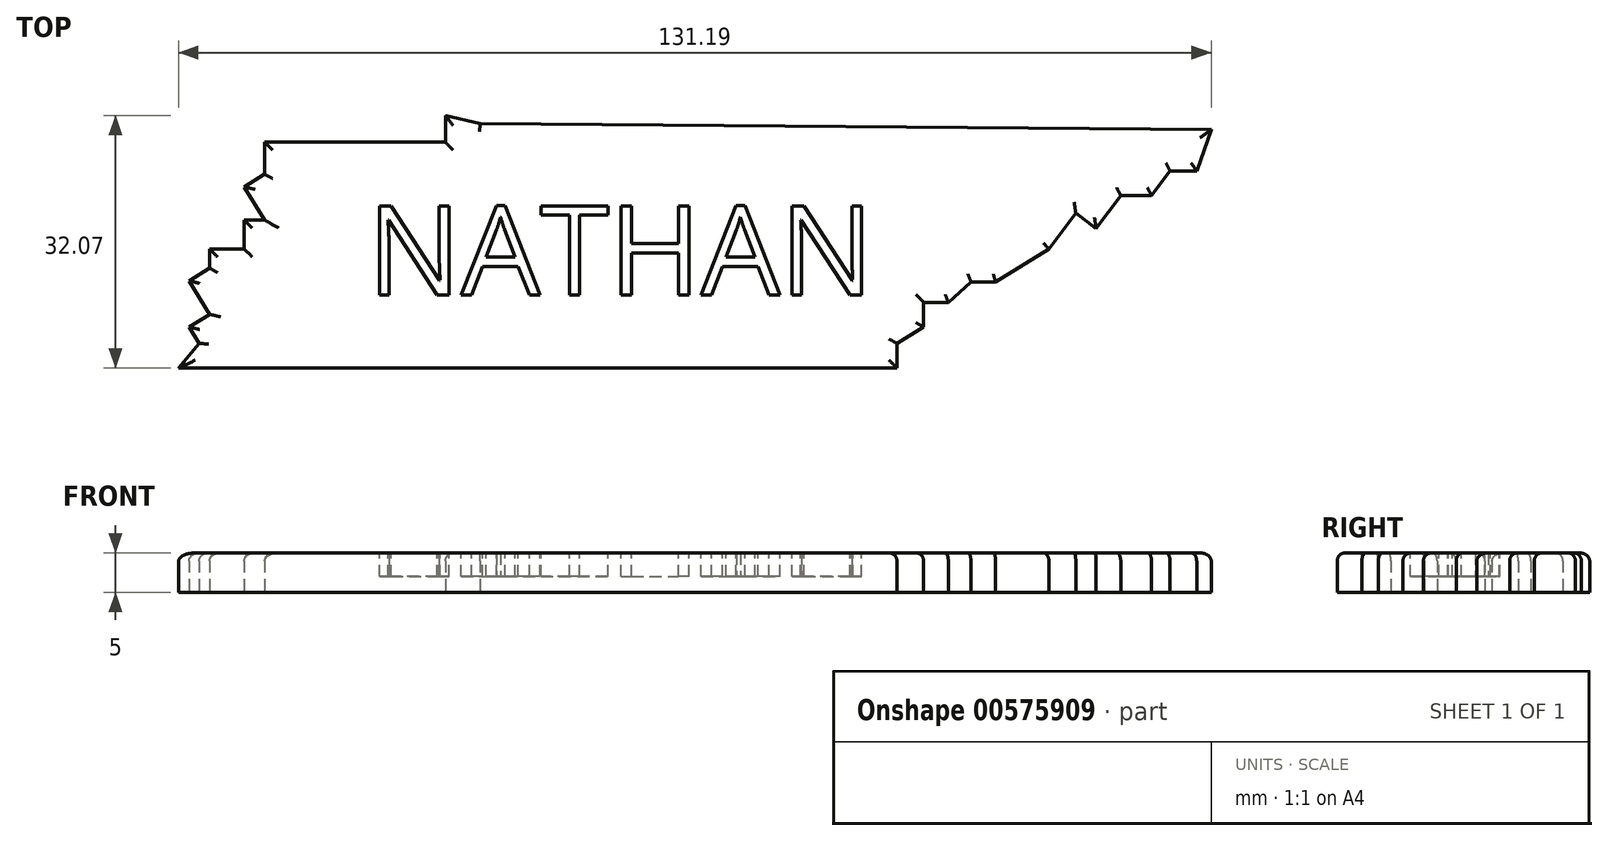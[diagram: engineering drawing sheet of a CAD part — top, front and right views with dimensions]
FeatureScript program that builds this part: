
annotation { "Feature Type Name" : "Feature", "Feature Type Description" : "" }
export const myFeature = defineFeature(function(context is Context, id is Id, definition is map)
    precondition{}
    {
        {
            var Q0;
            Q0=qCreatedBy(makeId("Top.planeOp"),FACE);
            var sketch = newSketch(context, id + "F0", { "sketchPlane" : qUnion([Q0])});
            skLineSegment(sketch, "E0", {"start": v(64.67, 9.9) * mm, "end": v(61.28, 9.9) * mm});
            skLineSegment(sketch, "E1", {"start": v(61.28, 9.9) * mm, "end": v(58.93, 6.78) * mm});
            skLineSegment(sketch, "E2", {"start": v(58.93, 6.78) * mm, "end": v(55.02, 6.78) * mm});
            skLineSegment(sketch, "E3", {"start": v(55.02, 6.78) * mm, "end": v(51.9, 2.6) * mm});
            skLineSegment(sketch, "E4", {"start": v(51.9, 2.6) * mm, "end": v(49.3, 4.55) * mm});
            skLineSegment(sketch, "E5", {"start": v(49.3, 4.55) * mm, "end": v(45.9, 0) * mm});
            skLineSegment(sketch, "E6", {"start": v(45.9, 0) * mm, "end": v(42.5, -2.09) * mm});
            skLineSegment(sketch, "E7", {"start": v(42.5, -2.09) * mm, "end": v(39.11, -4.17) * mm});
            skLineSegment(sketch, "E8", {"start": v(39.11, -4.17) * mm, "end": v(35.99, -4.17) * mm});
            skLineSegment(sketch, "E9", {"start": v(35.99, -4.17) * mm, "end": v(33.12, -6.78) * mm});
            skLineSegment(sketch, "E10", {"start": v(33.12, -6.78) * mm, "end": v(29.99, -6.78) * mm});
            skLineSegment(sketch, "E11", {"start": v(29.99, -6.78) * mm, "end": v(29.99, -9.9) * mm});
            skLineSegment(sketch, "E12", {"start": v(29.99, -9.9) * mm, "end": v(26.6, -12) * mm});
            skLineSegment(sketch, "E13", {"start": v(26.6, -12) * mm, "end": v(26.6, -15.12) * mm});
            skLineSegment(sketch, "E14", {"start": v(26.6, -15.12) * mm, "end": v(-64.67, -15.12) * mm});
            skLineSegment(sketch, "E15", {"start": v(-64.67, -15.12) * mm, "end": v(-62.06, -12) * mm});
            skLineSegment(sketch, "E16", {"start": v(-62.06, -12) * mm, "end": v(-63.35, -9.9) * mm});
            skLineSegment(sketch, "E17", {"start": v(-63.35, -9.9) * mm, "end": v(-60.73, -8.3) * mm});
            skLineSegment(sketch, "E18", {"start": v(-60.73, -8.3) * mm, "end": v(-63.35, -4.04) * mm});
            skLineSegment(sketch, "E19", {"start": v(-63.35, -4.04) * mm, "end": v(-60.73, -2.43) * mm});
            skLineSegment(sketch, "E20", {"start": v(-60.73, -2.43) * mm, "end": v(-60.73, 0) * mm});
            skLineSegment(sketch, "E21", {"start": v(-60.73, 0) * mm, "end": v(-56.32, 0) * mm});
            skLineSegment(sketch, "E22", {"start": v(-56.32, 0) * mm, "end": v(-56.32, 3.65) * mm});
            skLineSegment(sketch, "E23", {"start": v(-56.32, 3.65) * mm, "end": v(-53.72, 3.65) * mm});
            skLineSegment(sketch, "E24", {"start": v(-53.72, 3.65) * mm, "end": v(-55.02, 5.77) * mm});
            skLineSegment(sketch, "E25", {"start": v(-55.02, 5.77) * mm, "end": v(-56.32, 7.89) * mm});
            skLineSegment(sketch, "E26", {"start": v(-56.32, 7.89) * mm, "end": v(-53.72, 9.5) * mm});
            skLineSegment(sketch, "E27", {"start": v(-53.72, 9.5) * mm, "end": v(-53.72, 13.56) * mm});
            skLineSegment(sketch, "E28", {"start": v(-53.72, 13.56) * mm, "end": v(-30.77, 13.56) * mm});
            skLineSegment(sketch, "E29", {"start": v(-30.77, 13.56) * mm, "end": v(-30.77, 16.95) * mm});
            skLineSegment(sketch, "E30", {"start": v(-30.77, 16.95) * mm, "end": v(-26.34, 15.9) * mm});
            skLineSegment(sketch, "E31", {"start": v(64.67, 9.9) * mm, "end": v(66.52, 15.14) * mm});
            skLineSegment(sketch, "E32", {"start": v(66.52, 15.14) * mm, "end": v(-26.34, 15.9) * mm});
            skSolve(sketch);
        }
        {
            var Q0;
            Q0=makeQuery(id+"F0.imprint","IMPRINT",FACE,{"disambiguationData":[TD([[makeQuery(id+"F0.imprint","IMPRINT",EDGE,{"derivedFrom":sQuery(id+"F0.wireOp",EDGE,"E0")}),-1.0]])]});
            extrude(context, id + "F1", {"entities" : qUnion([Q0]), "depth" : 5 * mm, "offsetDistance" : 25 * mm});
        }
        {
            var Q0;
            Q0=makeQuery(id+"F1.opExtrude","CAP_EDGE",EDGE,{"disambiguationData":[OSD([sQuery(id+"F0.wireOp",EDGE,"E30")])],"isStart":false});
            var Q1;
            Q1=makeQuery(id+"F1.opExtrude","CAP_EDGE",EDGE,{"disambiguationData":[OSD([sQuery(id+"F0.wireOp",EDGE,"E28")])],"isStart":false});
            var Q2;
            Q2=makeQuery(id+"F1.opExtrude","CAP_EDGE",EDGE,{"disambiguationData":[OSD([sQuery(id+"F0.wireOp",EDGE,"E27")])],"isStart":false});
            var Q3;
            Q3=makeQuery(id+"F1.opExtrude","CAP_EDGE",EDGE,{"disambiguationData":[OSD([sQuery(id+"F0.wireOp",EDGE,"E26")])],"isStart":false});
            var Q4;
            Q4=makeQuery(id+"F1.opExtrude","CAP_EDGE",EDGE,{"disambiguationData":[OSD([sQuery(id+"F0.wireOp",EDGE,"E24"),sQuery(id+"F0.wireOp",EDGE,"E25")])],"isStart":false});
            var Q5;
            Q5=makeQuery(id+"F1.opExtrude","CAP_EDGE",EDGE,{"disambiguationData":[OSD([sQuery(id+"F0.wireOp",EDGE,"E29")])],"isStart":false});
            var Q6;
            Q6=makeQuery(id+"F1.opExtrude","CAP_EDGE",EDGE,{"disambiguationData":[OSD([sQuery(id+"F0.wireOp",EDGE,"E32")])],"isStart":false});
            var Q7;
            Q7=makeQuery(id+"F1.opExtrude","CAP_EDGE",EDGE,{"disambiguationData":[OSD([sQuery(id+"F0.wireOp",EDGE,"E23")])],"isStart":false});
            var Q8;
            Q8=makeQuery(id+"F1.opExtrude","CAP_EDGE",EDGE,{"disambiguationData":[OSD([sQuery(id+"F0.wireOp",EDGE,"E22")])],"isStart":false});
            var Q9;
            Q9=makeQuery(id+"F1.opExtrude","CAP_EDGE",EDGE,{"disambiguationData":[OSD([sQuery(id+"F0.wireOp",EDGE,"E21")])],"isStart":false});
            var Q10;
            Q10=makeQuery(id+"F1.opExtrude","CAP_EDGE",EDGE,{"disambiguationData":[OSD([sQuery(id+"F0.wireOp",EDGE,"E20")])],"isStart":false});
            var Q11;
            Q11=makeQuery(id+"F1.opExtrude","CAP_EDGE",EDGE,{"disambiguationData":[OSD([sQuery(id+"F0.wireOp",EDGE,"E19")])],"isStart":false});
            var Q12;
            Q12=makeQuery(id+"F1.opExtrude","CAP_EDGE",EDGE,{"disambiguationData":[OSD([sQuery(id+"F0.wireOp",EDGE,"E18")])],"isStart":false});
            var Q13;
            Q13=makeQuery(id+"F1.opExtrude","CAP_EDGE",EDGE,{"disambiguationData":[OSD([sQuery(id+"F0.wireOp",EDGE,"E17")])],"isStart":false});
            var Q14;
            Q14=makeQuery(id+"F1.opExtrude","CAP_EDGE",EDGE,{"disambiguationData":[OSD([sQuery(id+"F0.wireOp",EDGE,"E16")])],"isStart":false});
            var Q15;
            Q15=makeQuery(id+"F1.opExtrude","CAP_EDGE",EDGE,{"disambiguationData":[OSD([sQuery(id+"F0.wireOp",EDGE,"E15")])],"isStart":false});
            var Q16;
            Q16=makeQuery(id+"F1.opExtrude","CAP_EDGE",EDGE,{"disambiguationData":[OSD([sQuery(id+"F0.wireOp",EDGE,"E14")])],"isStart":false});
            var Q17;
            Q17=makeQuery(id+"F1.opExtrude","CAP_EDGE",EDGE,{"disambiguationData":[OSD([sQuery(id+"F0.wireOp",EDGE,"E13")])],"isStart":false});
            var Q18;
            Q18=makeQuery(id+"F1.opExtrude","CAP_EDGE",EDGE,{"disambiguationData":[OSD([sQuery(id+"F0.wireOp",EDGE,"E12")])],"isStart":false});
            var Q19;
            Q19=makeQuery(id+"F1.opExtrude","CAP_EDGE",EDGE,{"disambiguationData":[OSD([sQuery(id+"F0.wireOp",EDGE,"E11")])],"isStart":false});
            var Q20;
            Q20=makeQuery(id+"F1.opExtrude","CAP_EDGE",EDGE,{"disambiguationData":[OSD([sQuery(id+"F0.wireOp",EDGE,"E10")])],"isStart":false});
            var Q21;
            Q21=makeQuery(id+"F1.opExtrude","CAP_EDGE",EDGE,{"disambiguationData":[OSD([sQuery(id+"F0.wireOp",EDGE,"E9")])],"isStart":false});
            var Q22;
            Q22=makeQuery(id+"F1.opExtrude","CAP_EDGE",EDGE,{"disambiguationData":[OSD([sQuery(id+"F0.wireOp",EDGE,"E8")])],"isStart":false});
            var Q23;
            Q23=makeQuery(id+"F1.opExtrude","CAP_EDGE",EDGE,{"disambiguationData":[OSD([sQuery(id+"F0.wireOp",EDGE,"E6"),sQuery(id+"F0.wireOp",EDGE,"E7")])],"isStart":false});
            var Q24;
            Q24=makeQuery(id+"F1.opExtrude","CAP_EDGE",EDGE,{"disambiguationData":[OSD([sQuery(id+"F0.wireOp",EDGE,"E5")])],"isStart":false});
            var Q25;
            Q25=makeQuery(id+"F1.opExtrude","CAP_EDGE",EDGE,{"disambiguationData":[OSD([sQuery(id+"F0.wireOp",EDGE,"E4")])],"isStart":false});
            var Q26;
            Q26=makeQuery(id+"F1.opExtrude","CAP_EDGE",EDGE,{"disambiguationData":[OSD([sQuery(id+"F0.wireOp",EDGE,"E3")])],"isStart":false});
            var Q27;
            Q27=makeQuery(id+"F1.opExtrude","CAP_EDGE",EDGE,{"disambiguationData":[OSD([sQuery(id+"F0.wireOp",EDGE,"E2")])],"isStart":false});
            var Q28;
            Q28=makeQuery(id+"F1.opExtrude","CAP_EDGE",EDGE,{"disambiguationData":[OSD([sQuery(id+"F0.wireOp",EDGE,"E1")])],"isStart":false});
            var Q29;
            Q29=makeQuery(id+"F1.opExtrude","CAP_EDGE",EDGE,{"disambiguationData":[OSD([sQuery(id+"F0.wireOp",EDGE,"E0")])],"isStart":false});
            var Q30;
            Q30=makeQuery(id+"F1.opExtrude","CAP_EDGE",EDGE,{"disambiguationData":[OSD([sQuery(id+"F0.wireOp",EDGE,"E31")])],"isStart":false});
            fillet(context, id + "F2", {"entities" : qUnion([Q0, Q1, Q2, Q3, Q4, Q5, Q6, Q7, Q8, Q9, Q10, Q11, Q12, Q13, Q14, Q15, Q16, Q17, Q18, Q19, Q20, Q21, Q22, Q23, Q24, Q25, Q26, Q27, Q28, Q29, Q30]), "radius" : 1 * mm, "tangentPropagation" : true, "allowEdgeOverflow" : false});
        }
        {
            var Q0;
            Q0=makeQuery(id+"F1.opExtrude","CAP_FACE",FACE,{"disambiguationData":[OSD([sQuery(id+"F0.wireOp",EDGE,"E0"),sQuery(id+"F0.wireOp",EDGE,"E1"),sQuery(id+"F0.wireOp",EDGE,"E2"),sQuery(id+"F0.wireOp",EDGE,"E3"),sQuery(id+"F0.wireOp",EDGE,"E4"),sQuery(id+"F0.wireOp",EDGE,"E5"),sQuery(id+"F0.wireOp",EDGE,"E6"),sQuery(id+"F0.wireOp",EDGE,"E7"),sQuery(id+"F0.wireOp",EDGE,"E8"),sQuery(id+"F0.wireOp",EDGE,"E9"),sQuery(id+"F0.wireOp",EDGE,"E10"),sQuery(id+"F0.wireOp",EDGE,"E11"),sQuery(id+"F0.wireOp",EDGE,"E12"),sQuery(id+"F0.wireOp",EDGE,"E13"),sQuery(id+"F0.wireOp",EDGE,"E14"),sQuery(id+"F0.wireOp",EDGE,"E15"),sQuery(id+"F0.wireOp",EDGE,"E16"),sQuery(id+"F0.wireOp",EDGE,"E17"),sQuery(id+"F0.wireOp",EDGE,"E18"),sQuery(id+"F0.wireOp",EDGE,"E19"),sQuery(id+"F0.wireOp",EDGE,"E20"),sQuery(id+"F0.wireOp",EDGE,"E21"),sQuery(id+"F0.wireOp",EDGE,"E22"),sQuery(id+"F0.wireOp",EDGE,"E23"),sQuery(id+"F0.wireOp",EDGE,"E24"),sQuery(id+"F0.wireOp",EDGE,"E25"),sQuery(id+"F0.wireOp",EDGE,"E26"),sQuery(id+"F0.wireOp",EDGE,"E27"),sQuery(id+"F0.wireOp",EDGE,"E28"),sQuery(id+"F0.wireOp",EDGE,"E29"),sQuery(id+"F0.wireOp",EDGE,"E30"),sQuery(id+"F0.wireOp",EDGE,"E31"),sQuery(id+"F0.wireOp",EDGE,"E32")])],"isStart":false});
            var sketch = newSketch(context, id + "F3", { "sketchPlane" : qUnion([Q0])});
            skText(sketch, "E33", { "text": "NATHAN", "fontName": "OpenSans-Regular.ttf"});
            const initialGuessF3  = {"E33": [-0.0407, -0.00583, 1, 0, 0.0114]};
            skSetInitialGuess(sketch, initialGuessF3);
            skSolve(sketch);
        }
        {
            var Q0;
            Q0 = qSketchRegion(id + "F3", true);
            extrude(context, id + "F4", {"entities" : qUnion([Q0]), "operationType" : NewBodyOperationType.REMOVE, "oppositeDirection" : true, "depth" : 3 * mm, "offsetDistance" : 25 * mm});
        }
    });
